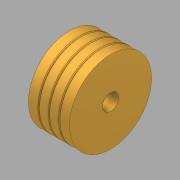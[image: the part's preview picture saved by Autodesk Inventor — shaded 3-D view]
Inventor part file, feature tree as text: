
AUTODESK INVENTOR PART (.ipt)
format: ipt  version: 2020 (Build 240168000, 168)  size: 126,464 bytes
history: native  units: in
note: dims shown in document units (in); Inventor stores cm internally (conversion verified against a paired STEP export)
features: sketch x2, other x1, revolve x1, hole x1
ambient origin geometry x8: Origin, YZ Plane, XZ Plane, XY Plane, X Axis, Y Axis, Z Axis, Center Point
bodies: Body1 (feature_tree)
feature tree (5):
  other  "Sólido1"
  revolve  "Revolución1"  [1 undecoded]
  hole  "Agujero1"  [1 undecoded]
  sketch  "Boceto1"  dims[d0=0.25in d1=0.25in]
  sketch  "Boceto2"  dims[d3=0.0625in d6=0.0625in d7=0.0625in d12=90.0deg d13=0.0764in d14=0.25in d15=0.099in d16=0.125in d17=0.5635in d18=0.302in d19=0.8108in d20=0.005in]
note: 2 required parameter values undecoded (feature->parameter linkage not recoverable at this tier; creation-order binding heuristic only, values carry confidence <= 0.55)